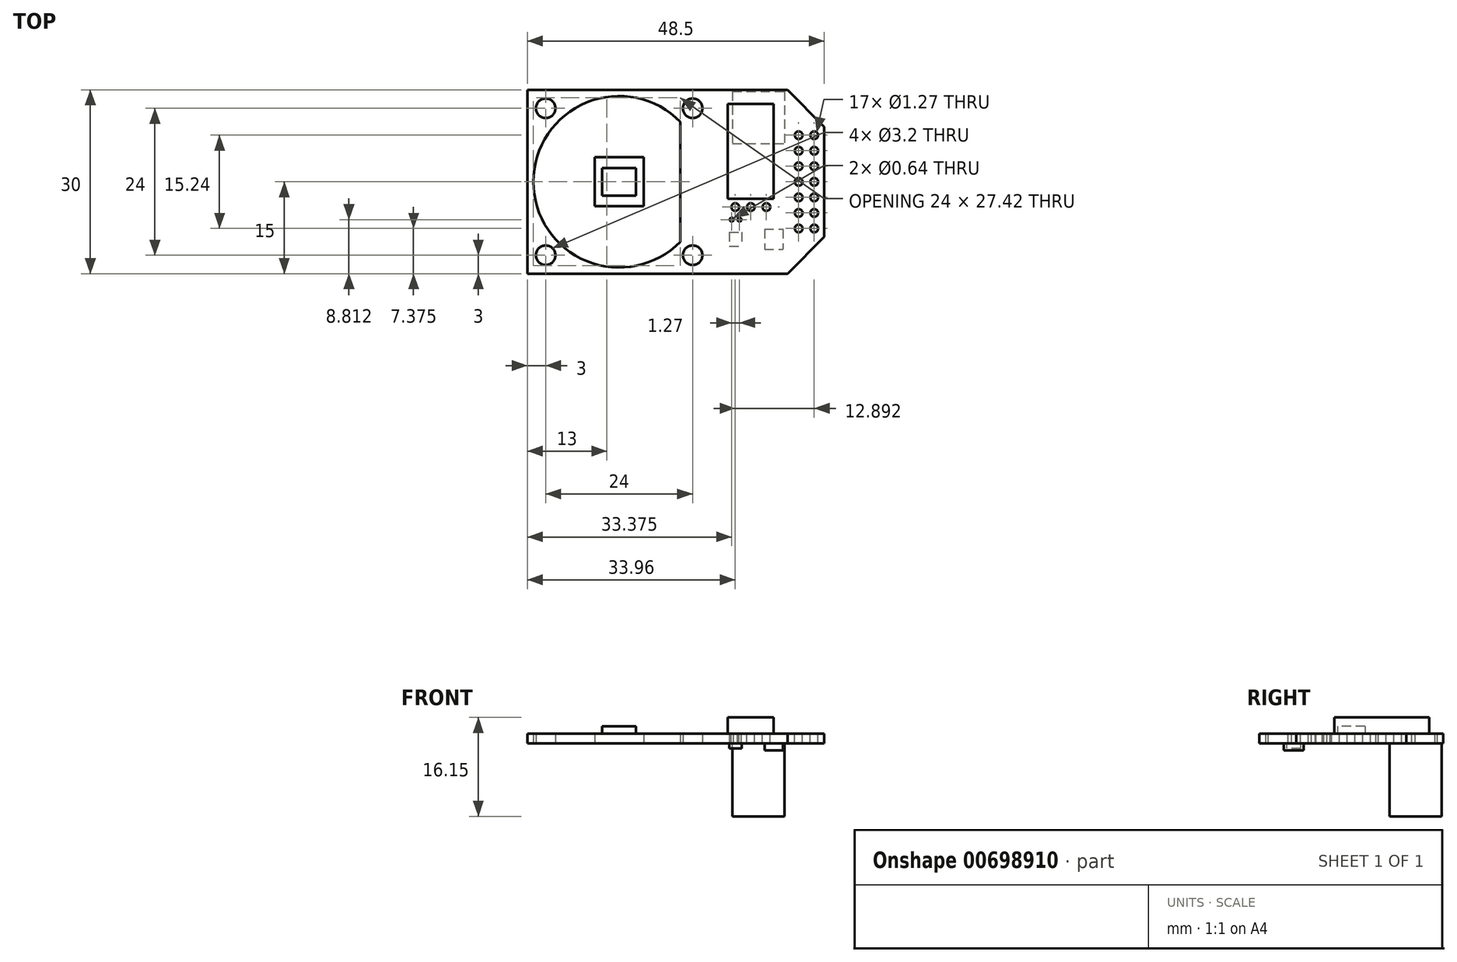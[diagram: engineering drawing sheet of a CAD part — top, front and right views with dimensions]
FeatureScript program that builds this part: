
annotation { "Feature Type Name" : "Feature", "Feature Type Description" : "" }
export const myFeature = defineFeature(function(context is Context, id is Id, definition is map)
    precondition{}
    {
        {
            var Q0;
            Q0=qCreatedBy(makeId("Top.planeOp"),FACE);
            var sketch = newSketch(context, id + "F0", { "sketchPlane" : qUnion([Q0])});
            skLineSegment(sketch, "E0", {"start": v(-15, -15) * mm, "end": v(-15, 15) * mm});
            skLineSegment(sketch, "E1", {"start": v(-15, 15) * mm, "end": v(27.5, 15) * mm});
            skLineSegment(sketch, "E2", {"start": v(27.5, 15) * mm, "end": v(33.5, 9) * mm});
            skLineSegment(sketch, "E3", {"start": v(33.5, 9) * mm, "end": v(33.5, -9) * mm});
            skLineSegment(sketch, "E4", {"start": v(33.5, -9) * mm, "end": v(27.5, -15) * mm});
            skLineSegment(sketch, "E5", {"start": v(27.5, -15) * mm, "end": v(-15, -15) * mm});
            skPoint(sketch, "E6", {"position": v(33.5, 0) * mm});
            skLineSegment(sketch, "E7.bottom", {"start": v(12, 12) * mm, "end": v(-12, 12) * mm, "construction": true});
            skLineSegment(sketch, "E7.top", {"start": v(12, -12) * mm, "end": v(-12, -12) * mm, "construction": true});
            skLineSegment(sketch, "E7.left", {"start": v(12, 12) * mm, "end": v(12, -12) * mm, "construction": true});
            skLineSegment(sketch, "E7.right", {"start": v(-12, 12) * mm, "end": v(-12, -12) * mm, "construction": true});
            skPoint(sketch, "E7.middle", {"position": v(0, 0) * mm});
            skCircle(sketch, "E8", {"center": v(-12, 12) * mm, "radius": 1.6 * mm});
            skCircle(sketch, "E9", {"center": v(12, 12) * mm, "radius": 1.6 * mm});
            skCircle(sketch, "E10", {"center": v(12, -12) * mm, "radius": 1.6 * mm});
            skCircle(sketch, "E11", {"center": v(-12, -12) * mm, "radius": 1.6 * mm});
            skLineSegment(sketch, "E12.bottom", {"start": v(4, 4) * mm, "end": v(-4, 4) * mm});
            skLineSegment(sketch, "E12.top", {"start": v(4, -4) * mm, "end": v(-4, -4) * mm});
            skLineSegment(sketch, "E12.left", {"start": v(4, 4) * mm, "end": v(4, -4) * mm});
            skLineSegment(sketch, "E12.right", {"start": v(-4, 4) * mm, "end": v(-4, -4) * mm});
            skLineSegment(sketch, "E13.bottom", {"start": v(14, 2) * mm, "end": v(4, 2) * mm});
            skLineSegment(sketch, "E13.top", {"start": v(14, -2) * mm, "end": v(4, -2) * mm});
            skLineSegment(sketch, "E13.left", {"start": v(14, 2) * mm, "end": v(14, -2) * mm});
            skLineSegment(sketch, "E13.right", {"start": v(4, 2) * mm, "end": v(4, -2) * mm});
            skPoint(sketch, "E13.middle", {"position": v(9, 0) * mm});
            skCircle(sketch, "E14", {"center": v(0, 0) * mm, "radius": 14 * mm});
            skLineSegment(sketch, "E15", {"start": v(10, 9.8) * mm, "end": v(10, -9.8) * mm});
            skSolve(sketch);
        }
        {
            var Q0;
            {var subQ0=sQuery(id+"F0.wireOp",EDGE,"E13.right");Q0=makeQuery(id+"F0.imprint","IMPRINT",FACE,{"disambiguationData":[TD([[makeQuery(id+"F0.imprint","IMPRINT",EDGE,{"derivedFrom":subQ0}),1.0]])]});}
            var Q1;
            {var subQ0=sQuery(id+"F0.wireOp",EDGE,"E14");var subQ4=sQuery(id+"F0.wireOp",EDGE,"E13.bottom");var subQ5=makeQuery(id+"F0.imprint","INTERSECT",VERTEX,{"derivedFrom":[subQ4,subQ0]});Q1=makeQuery(id+"F0.imprint","IMPRINT",FACE,{"disambiguationData":[TD([[makeQuery(id+"F0.imprint","IMPRINT",EDGE,{"disambiguationData":[TD([[subQ5,-1.0]])],"derivedFrom":subQ4}),1.0]])]});}
            var Q2;
            Q2=makeQuery(id+"F0.imprint","IMPRINT",FACE,{"disambiguationData":[TD([[makeQuery(id+"F0.imprint","IMPRINT",EDGE,{"derivedFrom":sQuery(id+"F0.wireOp",EDGE,"E0")}),-1.0]])]});
            var Q3;
            {var subQ0=sQuery(id+"F0.wireOp",EDGE,"E13.left");var subQ1=sQuery(id+"F0.wireOp",EDGE,"E13.bottom");var subQ2=makeQuery(id+"F0.imprint","INTERSECT",VERTEX,{"derivedFrom":[subQ1,subQ0]});Q3=makeQuery(id+"F0.imprint","IMPRINT",FACE,{"disambiguationData":[TD([[makeQuery(id+"F0.imprint","IMPRINT",EDGE,{"disambiguationData":[TD([[subQ2,-1.0]])],"derivedFrom":subQ1}),1.0]])]});}
            var Q4;
            {var subQ0=sQuery(id+"F0.wireOp",EDGE,"E13.left");var subQ1=sQuery(id+"F0.wireOp",EDGE,"E13.top");var subQ2=makeQuery(id+"F0.imprint","INTERSECT",VERTEX,{"derivedFrom":[subQ1,subQ0]});Q4=makeQuery(id+"F0.imprint","IMPRINT",FACE,{"disambiguationData":[TD([[makeQuery(id+"F0.imprint","IMPRINT",EDGE,{"disambiguationData":[TD([[subQ2,-1.0]])],"derivedFrom":subQ1}),-1.0]])]});}
            var Q5;
            {var subQ3=sQuery(id+"F0.wireOp",EDGE,"E12.bottom");Q5=makeQuery(id+"F0.imprint","IMPRINT",FACE,{"disambiguationData":[TD([[makeQuery(id+"F0.imprint","IMPRINT",EDGE,{"derivedFrom":subQ3}),1.0]])]});}
            var Q6;
            {var subQ0=sQuery(id+"F0.wireOp",EDGE,"E14");var subQ1=sQuery(id+"F0.wireOp",EDGE,"E13.bottom");var subQ2=makeQuery(id+"F0.imprint","INTERSECT",VERTEX,{"derivedFrom":[subQ1,subQ0]});Q6=makeQuery(id+"F0.imprint","IMPRINT",FACE,{"disambiguationData":[TD([[makeQuery(id+"F0.imprint","IMPRINT",EDGE,{"disambiguationData":[TD([[subQ2,-1.0]])],"derivedFrom":subQ1}),-1.0]])]});}
            var Q7;
            {var subQ0=sQuery(id+"F0.wireOp",EDGE,"E14");var subQ1=sQuery(id+"F0.wireOp",EDGE,"E13.top");var subQ2=makeQuery(id+"F0.imprint","INTERSECT",VERTEX,{"derivedFrom":[subQ1,subQ0]});Q7=makeQuery(id+"F0.imprint","IMPRINT",FACE,{"disambiguationData":[TD([[makeQuery(id+"F0.imprint","IMPRINT",EDGE,{"disambiguationData":[TD([[subQ2,-1.0]])],"derivedFrom":subQ1}),1.0]])]});}
            extrude(context, id + "F1", {"entities" : qUnion([Q0, Q1, Q2, Q3, Q4, Q5, Q6, Q7]), "depth" : 1.6 * mm});
        }
        {
            var Q0;
            Q0=makeQuery(id+"F1.opExtrude","CAP_FACE",FACE,{"disambiguationData":[OSD([sQuery(id+"F0.wireOp",EDGE,"E0"),sQuery(id+"F0.wireOp",EDGE,"E1"),sQuery(id+"F0.wireOp",EDGE,"E2"),sQuery(id+"F0.wireOp",EDGE,"E3"),sQuery(id+"F0.wireOp",EDGE,"E4"),sQuery(id+"F0.wireOp",EDGE,"E5"),sQuery(id+"F0.wireOp",EDGE,"E8"),sQuery(id+"F0.wireOp",EDGE,"E9"),sQuery(id+"F0.wireOp",EDGE,"E10"),sQuery(id+"F0.wireOp",EDGE,"E11"),sQuery(id+"F0.wireOp",EDGE,"E12.bottom"),sQuery(id+"F0.wireOp",EDGE,"E12.top"),sQuery(id+"F0.wireOp",EDGE,"E12.left"),sQuery(id+"F0.wireOp",EDGE,"E12.right"),sQuery(id+"F0.wireOp",EDGE,"E13.bottom"),sQuery(id+"F0.wireOp",EDGE,"E13.top"),sQuery(id+"F0.wireOp",EDGE,"E14"),sQuery(id+"F0.wireOp",EDGE,"E15")])],"isStart":false});
            var sketch = newSketch(context, id + "F2", { "sketchPlane" : qUnion([Q0])});
            skLineSegment(sketch, "E16.bottom", {"start": v(2.75, 2.25) * mm, "end": v(-2.75, 2.25) * mm});
            skLineSegment(sketch, "E16.top", {"start": v(2.75, -2.25) * mm, "end": v(-2.75, -2.25) * mm});
            skLineSegment(sketch, "E16.left", {"start": v(2.75, 2.25) * mm, "end": v(2.75, -2.25) * mm});
            skLineSegment(sketch, "E16.right", {"start": v(-2.75, 2.25) * mm, "end": v(-2.75, -2.25) * mm});
            skPoint(sketch, "E16.middle", {"position": v(0, 0) * mm});
            skLineSegment(sketch, "E17.bottom", {"start": v(25.25, 12.75) * mm, "end": v(17.75, 12.75) * mm});
            skLineSegment(sketch, "E17.top", {"start": v(25.25, -2.75) * mm, "end": v(17.75, -2.75) * mm});
            skLineSegment(sketch, "E17.left", {"start": v(25.25, 12.75) * mm, "end": v(25.25, -2.75) * mm});
            skLineSegment(sketch, "E17.right", {"start": v(17.75, 12.75) * mm, "end": v(17.75, -2.75) * mm});
            skPoint(sketch, "E17.middle", {"position": v(21.5, 5) * mm});
            skCircle(sketch, "E18", {"center": v(18.96, -4.13) * mm, "radius": 0.64 * mm});
            skCircle(sketch, "E19", {"center": v(21.5, -4.13) * mm, "radius": 0.64 * mm});
            skCircle(sketch, "E20", {"center": v(24.04, -4.13) * mm, "radius": 0.64 * mm});
            skLineSegment(sketch, "E21", {"start": v(18.96, -4.13) * mm, "end": v(21.5, -4.13) * mm, "construction": true});
            skLineSegment(sketch, "E22", {"start": v(21.5, -4.13) * mm, "end": v(24.04, -4.13) * mm, "construction": true});
            skCircle(sketch, "E23", {"center": v(29.31, 7.61) * mm, "radius": 0.64 * mm});
            skCircle(sketch, "E24.1.0.0", {"center": v(29.31, 5.07) * mm, "radius": 0.64 * mm});
            skCircle(sketch, "E24.2.0.0", {"center": v(29.31, 2.53) * mm, "radius": 0.64 * mm});
            skCircle(sketch, "E24.3.0.0", {"center": v(29.31, 0) * mm, "radius": 0.64 * mm});
            skCircle(sketch, "E24.4.0.0", {"center": v(29.31, -2.55) * mm, "radius": 0.64 * mm});
            skCircle(sketch, "E24.5.0.0", {"center": v(29.31, -5.09) * mm, "radius": 0.64 * mm});
            skCircle(sketch, "E24.6.0.0", {"center": v(29.31, -7.63) * mm, "radius": 0.64 * mm});
            skLineSegment(sketch, "E24.direction1", {"start": v(29.31, 7.61) * mm, "end": v(29.31, 5.07) * mm, "construction": true});
            skCircle(sketch, "E25.1.0.0", {"center": v(31.85, -2.55) * mm, "radius": 0.64 * mm});
            skCircle(sketch, "E25.1.0.1", {"center": v(31.85, 7.61) * mm, "radius": 0.64 * mm});
            skCircle(sketch, "E25.1.0.2", {"center": v(31.85, 5.07) * mm, "radius": 0.64 * mm});
            skCircle(sketch, "E25.1.0.3", {"center": v(31.85, 2.53) * mm, "radius": 0.64 * mm});
            skCircle(sketch, "E25.1.0.4", {"center": v(31.85, -7.63) * mm, "radius": 0.64 * mm});
            skCircle(sketch, "E25.1.0.5", {"center": v(31.85, 0) * mm, "radius": 0.64 * mm});
            skCircle(sketch, "E25.1.0.6", {"center": v(31.85, -5.09) * mm, "radius": 0.64 * mm});
            skLineSegment(sketch, "E25.1.0.7", {"start": v(31.85, 7.61) * mm, "end": v(31.85, 5.07) * mm, "construction": true});
            skLineSegment(sketch, "E25.direction1", {"start": v(29.31, -7.63) * mm, "end": v(31.85, -7.63) * mm, "construction": true});
            skCircle(sketch, "E26", {"center": v(18.38, -6.19) * mm, "radius": 0.32 * mm});
            skCircle(sketch, "E27", {"center": v(19.65, -6.19) * mm, "radius": 0.32 * mm});
            skSolve(sketch);
        }
        {
            var Q0;
            Q0=makeQuery(id+"F2.imprint","IMPRINT",FACE,{"disambiguationData":[TD([[makeQuery(id+"F2.imprint","IMPRINT",EDGE,{"derivedFrom":sQuery(id+"F2.wireOp",EDGE,"E16.bottom")}),1.0]])]});
            extrude(context, id + "F3", {"entities" : qUnion([Q0]), "operationType" : NewBodyOperationType.ADD, "depth" : 1.2 * mm});
        }
        {
            var Q0;
            Q0=makeQuery(id+"F2.imprint","IMPRINT",FACE,{"disambiguationData":[TD([[makeQuery(id+"F2.imprint","IMPRINT",EDGE,{"derivedFrom":sQuery(id+"F2.wireOp",EDGE,"E17.bottom")}),1.0]])]});
            extrude(context, id + "F4", {"entities" : qUnion([Q0]), "operationType" : NewBodyOperationType.ADD, "depth" : 2.65 * mm});
        }
        {
            var Q0;
            Q0=makeQuery(id+"F2.imprint","IMPRINT",FACE,{"disambiguationData":[TD([[makeQuery(id+"F2.imprint","IMPRINT",EDGE,{"derivedFrom":sQuery(id+"F2.wireOp",EDGE,"E18")}),1.0]])]});
            var Q1;
            Q1=makeQuery(id+"F2.imprint","IMPRINT",FACE,{"disambiguationData":[TD([[makeQuery(id+"F2.imprint","IMPRINT",EDGE,{"derivedFrom":sQuery(id+"F2.wireOp",EDGE,"E19")}),1.0]])]});
            var Q2;
            Q2=makeQuery(id+"F2.imprint","IMPRINT",FACE,{"disambiguationData":[TD([[makeQuery(id+"F2.imprint","IMPRINT",EDGE,{"derivedFrom":sQuery(id+"F2.wireOp",EDGE,"E20")}),1.0]])]});
            var Q3;
            Q3=makeQuery(id+"F2.imprint","IMPRINT",FACE,{"disambiguationData":[TD([[makeQuery(id+"F2.imprint","IMPRINT",EDGE,{"derivedFrom":sQuery(id+"F2.wireOp",EDGE,"E27")}),1.0]])]});
            var Q4;
            Q4=makeQuery(id+"F2.imprint","IMPRINT",FACE,{"disambiguationData":[TD([[makeQuery(id+"F2.imprint","IMPRINT",EDGE,{"derivedFrom":sQuery(id+"F2.wireOp",EDGE,"E26")}),1.0]])]});
            var Q5;
            Q5=makeQuery(id+"F2.imprint","IMPRINT",FACE,{"disambiguationData":[TD([[makeQuery(id+"F2.imprint","IMPRINT",EDGE,{"derivedFrom":sQuery(id+"F2.wireOp",EDGE,"E24.6.0.0")}),1.0]])]});
            var Q6;
            Q6=makeQuery(id+"F2.imprint","IMPRINT",FACE,{"disambiguationData":[TD([[makeQuery(id+"F2.imprint","IMPRINT",EDGE,{"derivedFrom":sQuery(id+"F2.wireOp",EDGE,"E25.1.0.4")}),1.0]])]});
            var Q7;
            Q7=makeQuery(id+"F2.imprint","IMPRINT",FACE,{"disambiguationData":[TD([[makeQuery(id+"F2.imprint","IMPRINT",EDGE,{"derivedFrom":sQuery(id+"F2.wireOp",EDGE,"E25.1.0.6")}),1.0]])]});
            var Q8;
            Q8=makeQuery(id+"F2.imprint","IMPRINT",FACE,{"disambiguationData":[TD([[makeQuery(id+"F2.imprint","IMPRINT",EDGE,{"derivedFrom":sQuery(id+"F2.wireOp",EDGE,"E24.5.0.0")}),1.0]])]});
            var Q9;
            Q9=makeQuery(id+"F2.imprint","IMPRINT",FACE,{"disambiguationData":[TD([[makeQuery(id+"F2.imprint","IMPRINT",EDGE,{"derivedFrom":sQuery(id+"F2.wireOp",EDGE,"E24.4.0.0")}),1.0]])]});
            var Q10;
            Q10=makeQuery(id+"F2.imprint","IMPRINT",FACE,{"disambiguationData":[TD([[makeQuery(id+"F2.imprint","IMPRINT",EDGE,{"derivedFrom":sQuery(id+"F2.wireOp",EDGE,"E25.1.0.0")}),1.0]])]});
            var Q11;
            Q11=makeQuery(id+"F2.imprint","IMPRINT",FACE,{"disambiguationData":[TD([[makeQuery(id+"F2.imprint","IMPRINT",EDGE,{"derivedFrom":sQuery(id+"F2.wireOp",EDGE,"E25.1.0.5")}),1.0]])]});
            var Q12;
            Q12=makeQuery(id+"F2.imprint","IMPRINT",FACE,{"disambiguationData":[TD([[makeQuery(id+"F2.imprint","IMPRINT",EDGE,{"derivedFrom":sQuery(id+"F2.wireOp",EDGE,"E24.3.0.0")}),1.0]])]});
            var Q13;
            Q13=makeQuery(id+"F2.imprint","IMPRINT",FACE,{"disambiguationData":[TD([[makeQuery(id+"F2.imprint","IMPRINT",EDGE,{"derivedFrom":sQuery(id+"F2.wireOp",EDGE,"E24.2.0.0")}),1.0]])]});
            var Q14;
            Q14=makeQuery(id+"F2.imprint","IMPRINT",FACE,{"disambiguationData":[TD([[makeQuery(id+"F2.imprint","IMPRINT",EDGE,{"derivedFrom":sQuery(id+"F2.wireOp",EDGE,"E25.1.0.3")}),1.0]])]});
            var Q15;
            Q15=makeQuery(id+"F2.imprint","IMPRINT",FACE,{"disambiguationData":[TD([[makeQuery(id+"F2.imprint","IMPRINT",EDGE,{"derivedFrom":sQuery(id+"F2.wireOp",EDGE,"E25.1.0.2")}),1.0]])]});
            var Q16;
            Q16=makeQuery(id+"F2.imprint","IMPRINT",FACE,{"disambiguationData":[TD([[makeQuery(id+"F2.imprint","IMPRINT",EDGE,{"derivedFrom":sQuery(id+"F2.wireOp",EDGE,"E24.1.0.0")}),1.0]])]});
            var Q17;
            Q17=makeQuery(id+"F2.imprint","IMPRINT",FACE,{"disambiguationData":[TD([[makeQuery(id+"F2.imprint","IMPRINT",EDGE,{"derivedFrom":sQuery(id+"F2.wireOp",EDGE,"E23")}),1.0]])]});
            var Q18;
            Q18=makeQuery(id+"F2.imprint","IMPRINT",FACE,{"disambiguationData":[TD([[makeQuery(id+"F2.imprint","IMPRINT",EDGE,{"derivedFrom":sQuery(id+"F2.wireOp",EDGE,"E25.1.0.1")}),1.0]])]});
            extrude(context, id + "F5", {"entities" : qUnion([Q0, Q1, Q2, Q3, Q4, Q5, Q6, Q7, Q8, Q9, Q10, Q11, Q12, Q13, Q14, Q15, Q16, Q17, Q18]), "operationType" : NewBodyOperationType.REMOVE, "oppositeDirection" : true, "depth" : 25 * mm});
        }
        {
            var Q0;
            Q0=makeQuery(id+"F1.opExtrude","CAP_FACE",FACE,{"disambiguationData":[OSD([sQuery(id+"F0.wireOp",EDGE,"E0"),sQuery(id+"F0.wireOp",EDGE,"E1"),sQuery(id+"F0.wireOp",EDGE,"E2"),sQuery(id+"F0.wireOp",EDGE,"E3"),sQuery(id+"F0.wireOp",EDGE,"E4"),sQuery(id+"F0.wireOp",EDGE,"E5"),sQuery(id+"F0.wireOp",EDGE,"E8"),sQuery(id+"F0.wireOp",EDGE,"E9"),sQuery(id+"F0.wireOp",EDGE,"E10"),sQuery(id+"F0.wireOp",EDGE,"E11"),sQuery(id+"F0.wireOp",EDGE,"E12.bottom"),sQuery(id+"F0.wireOp",EDGE,"E12.top"),sQuery(id+"F0.wireOp",EDGE,"E12.left"),sQuery(id+"F0.wireOp",EDGE,"E12.right"),sQuery(id+"F0.wireOp",EDGE,"E13.bottom"),sQuery(id+"F0.wireOp",EDGE,"E13.top"),sQuery(id+"F0.wireOp",EDGE,"E14"),sQuery(id+"F0.wireOp",EDGE,"E15")])],"isStart":true});
            var sketch = newSketch(context, id + "F6", { "sketchPlane" : qUnion([Q0])});
            skLineSegment(sketch, "E28.bottom", {"start": v(18.5, -14.75) * mm, "end": v(27, -14.75) * mm});
            skLineSegment(sketch, "E28.top", {"start": v(18.5, -6.25) * mm, "end": v(27, -6.25) * mm});
            skLineSegment(sketch, "E28.left", {"start": v(18.5, -14.75) * mm, "end": v(18.5, -6.25) * mm});
            skLineSegment(sketch, "E28.right", {"start": v(27, -14.75) * mm, "end": v(27, -6.25) * mm});
            skPoint(sketch, "E28.middle", {"position": v(22.75, -10.5) * mm});
            skLineSegment(sketch, "E29.bottom", {"start": v(23.75, 7.75) * mm, "end": v(26.75, 7.75) * mm});
            skLineSegment(sketch, "E29.top", {"start": v(23.75, 11) * mm, "end": v(26.75, 11) * mm});
            skLineSegment(sketch, "E29.left", {"start": v(23.75, 7.75) * mm, "end": v(23.75, 11) * mm});
            skLineSegment(sketch, "E29.right", {"start": v(26.75, 7.75) * mm, "end": v(26.75, 11) * mm});
            skPoint(sketch, "E29.middle", {"position": v(25.25, 9.38) * mm});
            skLineSegment(sketch, "E30.bottom", {"start": v(18, 8.25) * mm, "end": v(20, 8.25) * mm});
            skLineSegment(sketch, "E30.top", {"start": v(18, 10.5) * mm, "end": v(20, 10.5) * mm});
            skLineSegment(sketch, "E30.left", {"start": v(18, 8.25) * mm, "end": v(18, 10.5) * mm});
            skLineSegment(sketch, "E30.right", {"start": v(20, 8.25) * mm, "end": v(20, 10.5) * mm});
            skPoint(sketch, "E30.middle", {"position": v(19, 9.38) * mm});
            skSolve(sketch);
        }
        {
            var Q0;
            Q0=makeQuery(id+"F6.imprint","IMPRINT",FACE,{"disambiguationData":[TD([[makeQuery(id+"F6.imprint","IMPRINT",EDGE,{"derivedFrom":sQuery(id+"F6.wireOp",EDGE,"E28.bottom")}),1.0]])]});
            extrude(context, id + "F7", {"entities" : qUnion([Q0]), "operationType" : NewBodyOperationType.ADD, "depth" : 11.9 * mm});
        }
        {
            var Q0;
            Q0=makeQuery(id+"F6.imprint","IMPRINT",FACE,{"disambiguationData":[TD([[makeQuery(id+"F6.imprint","IMPRINT",EDGE,{"derivedFrom":sQuery(id+"F6.wireOp",EDGE,"E30.bottom")}),1.0]])]});
            extrude(context, id + "F8", {"entities" : qUnion([Q0]), "operationType" : NewBodyOperationType.ADD, "depth" : 0.8 * mm});
        }
        {
            var Q0;
            Q0=makeQuery(id+"F6.imprint","IMPRINT",FACE,{"disambiguationData":[TD([[makeQuery(id+"F6.imprint","IMPRINT",EDGE,{"derivedFrom":sQuery(id+"F6.wireOp",EDGE,"E29.bottom")}),1.0]])]});
            extrude(context, id + "F9", {"entities" : qUnion([Q0]), "operationType" : NewBodyOperationType.ADD, "depth" : 1.1 * mm});
        }
    });
